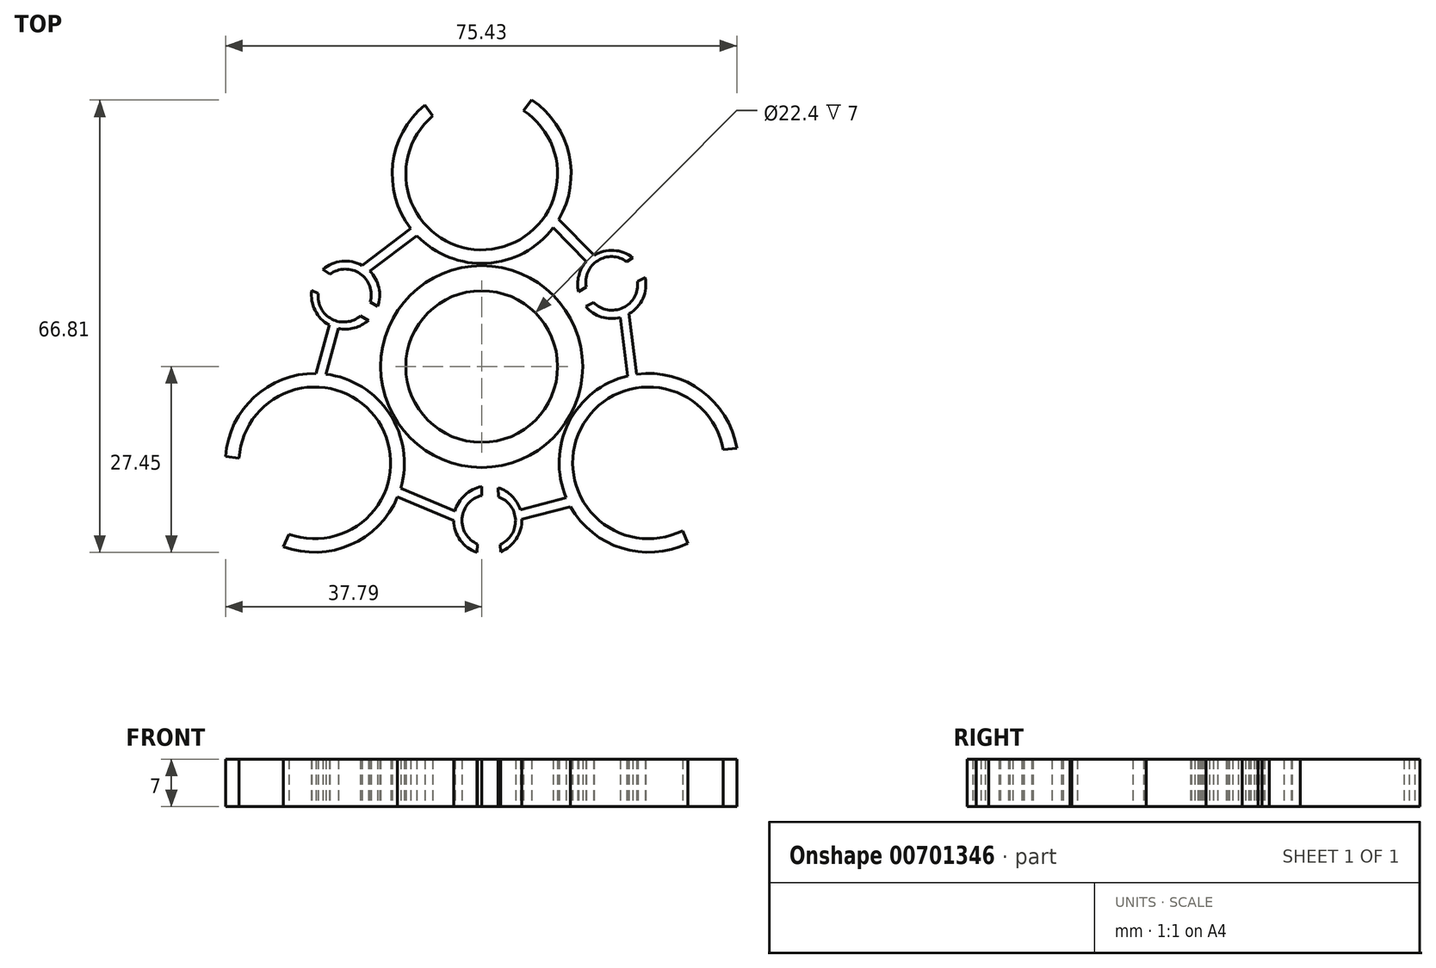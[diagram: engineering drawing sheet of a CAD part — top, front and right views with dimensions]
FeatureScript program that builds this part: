
annotation { "Feature Type Name" : "Feature", "Feature Type Description" : "" }
export const myFeature = defineFeature(function(context is Context, id is Id, definition is map)
    precondition{}
    {
        {
            var Q0;
            Q0=qCreatedBy(makeId("Top.planeOp"),FACE);
            var sketch = newSketch(context, id + "F0", { "sketchPlane" : qUnion([Q0])});
            skCircle(sketch, "E0", {"center": v(0, 0) * mm, "radius": 11.2 * mm});
            skArc(sketch, "E1", {"start": v(-7.22, 37) * mm, "mid": v(0.65, 17.25) * mm, "end": v(6.17, 37.78) * mm});
            skArc(sketch, "E2.1.0", {"start": v(-28.43, -24.75) * mm, "mid": v(-15.26, -8.06) * mm, "end": v(-35.8, -13.54) * mm});
            skArc(sketch, "E2.2.0", {"start": v(35.65, -12.25) * mm, "mid": v(14.61, -9.19) * mm, "end": v(29.63, -24.23) * mm});
            skArc(sketch, "E3", {"start": v(-8.4, 38.62) * mm, "mid": v(1.44, 15.3) * mm, "end": v(6, 40.2) * mm});
            skArc(sketch, "E4.1.0", {"start": v(-29.24, -26.58) * mm, "mid": v(-13.52, -7.08) * mm, "end": v(-37.79, -13.28) * mm});
            skArc(sketch, "E4.2.0", {"start": v(37.64, -12.04) * mm, "mid": v(12.9, -8.16) * mm, "end": v(30.4, -26.09) * mm});
            skCircle(sketch, "E5", {"center": v(0, 0) * mm, "radius": 14.9 * mm});
            skPoint(sketch, "E6", {"position": v(-6.05, 40.16) * mm});
            skPoint(sketch, "E7", {"position": v(3.9, 41.04) * mm});
            skPoint(sketch, "E8", {"position": v(3.9, 38.93) * mm});
            skPoint(sketch, "E9", {"position": v(-5.15, 38.37) * mm});
            skPoint(sketch, "E10.1.0", {"position": v(-31.76, -25.32) * mm});
            skPoint(sketch, "E10.1.1", {"position": v(-30.66, -23.65) * mm});
            skPoint(sketch, "E10.1.2", {"position": v(-35.67, -16.08) * mm});
            skPoint(sketch, "E10.1.3", {"position": v(-37.5, -17.14) * mm});
            skPoint(sketch, "E10.2.0", {"position": v(37.8, -14.84) * mm});
            skPoint(sketch, "E10.2.1", {"position": v(35.81, -14.72) * mm});
            skPoint(sketch, "E10.2.2", {"position": v(31.76, -22.85) * mm});
            skPoint(sketch, "E10.2.3", {"position": v(33.59, -23.9) * mm});
            skArc(sketch, "E11", {"start": v(-25.08, 11.26) * mm, "mid": v(-22.45, 6.1) * mm, "end": v(-16.7, 6.83) * mm});
            skArc(sketch, "E12.1.0", {"start": v(2.8, -27.35) * mm, "mid": v(5.94, -22.5) * mm, "end": v(2.44, -17.88) * mm});
            skArc(sketch, "E12.2.0", {"start": v(15.35, 8.86) * mm, "mid": v(21.39, 7.6) * mm, "end": v(24.12, 13.12) * mm});
            skLineSegment(sketch, "E13", {"start": v(-22.5, 6.14) * mm, "end": v(-24.46, -1.02) * mm});
            skLineSegment(sketch, "E14", {"start": v(-21.16, 5.64) * mm, "end": v(-23, -1.11) * mm});
            skLineSegment(sketch, "E15.1.0", {"start": v(5.7, -21.14) * mm, "end": v(12.47, -19.37) * mm});
            skLineSegment(sketch, "E15.1.1", {"start": v(5.94, -22.56) * mm, "end": v(13.1, -20.67) * mm});
            skLineSegment(sketch, "E15.2.0", {"start": v(15.46, 15.5) * mm, "end": v(10.54, 20.48) * mm});
            skLineSegment(sketch, "E15.2.1", {"start": v(16.56, 16.42) * mm, "end": v(11.35, 21.7) * mm});
            skLineSegment(sketch, "E16", {"start": v(-17.62, 14.94) * mm, "end": v(-10.45, 20.37) * mm});
            skLineSegment(sketch, "E17", {"start": v(-16.52, 14.1) * mm, "end": v(-9.56, 19.32) * mm});
            skLineSegment(sketch, "E18.1.0", {"start": v(-4.13, -22.73) * mm, "end": v(-12.42, -19.24) * mm});
            skLineSegment(sketch, "E18.1.1", {"start": v(-3.95, -21.36) * mm, "end": v(-11.96, -17.94) * mm});
            skLineSegment(sketch, "E18.2.0", {"start": v(21.75, 7.79) * mm, "end": v(22.87, -1.13) * mm});
            skLineSegment(sketch, "E18.2.1", {"start": v(20.48, 7.26) * mm, "end": v(21.51, -1.39) * mm});
            skPoint(sketch, "E19", {"position": v(-0.7, -27.45) * mm});
            skPoint(sketch, "E20", {"position": v(2.8, -27.35) * mm});
            skPoint(sketch, "E21", {"position": v(0, -17.73) * mm});
            skPoint(sketch, "E22", {"position": v(2.44, -17.88) * mm});
            skPoint(sketch, "E23.1.0", {"position": v(14.27, 11.06) * mm});
            skPoint(sketch, "E23.1.1", {"position": v(15.35, 8.86) * mm});
            skPoint(sketch, "E23.1.2", {"position": v(22.29, 16.09) * mm});
            skPoint(sketch, "E23.1.3", {"position": v(24.12, 13.12) * mm});
            skPoint(sketch, "E23.2.0", {"position": v(-16.7, 6.83) * mm});
            skPoint(sketch, "E23.2.1", {"position": v(-15.35, 8.86) * mm});
            skPoint(sketch, "E23.2.2", {"position": v(-25.08, 11.26) * mm});
            skPoint(sketch, "E23.2.3", {"position": v(-23.42, 14.33) * mm});
            skArc(sketch, "E24.trimOffspring", {"start": v(-15.35, 8.86) * mm, "mid": v(-17.27, 14.72) * mm, "end": v(-23.42, 14.33) * mm});
            skArc(sketch, "E25.trimOffspring", {"start": v(22.29, 16.09) * mm, "mid": v(16.51, 16.39) * mm, "end": v(14.27, 11.06) * mm});
            skArc(sketch, "E26.trimOffspring", {"start": v(0, -17.73) * mm, "mid": v(-4.12, -22.32) * mm, "end": v(-0.7, -27.45) * mm});
            skLineSegment(sketch, "E27", {"start": v(-23.42, 14.33) * mm, "end": v(-22.39, 13.63) * mm});
            skArc(sketch, "E28", {"start": v(-16.46, 9.53) * mm, "mid": v(-17.95, 13.72) * mm, "end": v(-22.39, 13.63) * mm});
            skLineSegment(sketch, "E29", {"start": v(-16.46, 9.53) * mm, "end": v(-15.35, 8.86) * mm});
            skLineSegment(sketch, "E30", {"start": v(-25.08, 11.26) * mm, "end": v(-24.1, 10.78) * mm});
            skArc(sketch, "E31", {"start": v(-24.1, 10.78) * mm, "mid": v(-22.12, 7.01) * mm, "end": v(-17.9, 7.49) * mm});
            skLineSegment(sketch, "E32", {"start": v(-17.9, 7.49) * mm, "end": v(-16.7, 6.83) * mm});
            skArc(sketch, "E33.1.0", {"start": v(-0.02, -19.03) * mm, "mid": v(-2.9, -22.4) * mm, "end": v(-0.6, -26.2) * mm});
            skLineSegment(sketch, "E33.1.1", {"start": v(-0.7, -27.45) * mm, "end": v(-0.6, -26.2) * mm});
            skLineSegment(sketch, "E33.1.2", {"start": v(-0.02, -19.03) * mm, "end": v(0, -17.73) * mm});
            skLineSegment(sketch, "E33.1.3", {"start": v(2.46, -19.24) * mm, "end": v(2.44, -17.88) * mm});
            skArc(sketch, "E33.1.4", {"start": v(2.72, -26.26) * mm, "mid": v(4.99, -22.66) * mm, "end": v(2.46, -19.24) * mm});
            skLineSegment(sketch, "E33.1.5", {"start": v(2.8, -27.35) * mm, "end": v(2.72, -26.26) * mm});
            skArc(sketch, "E33.2.0", {"start": v(16.49, 9.5) * mm, "mid": v(20.85, 8.69) * mm, "end": v(23, 12.57) * mm});
            skLineSegment(sketch, "E33.2.1", {"start": v(24.12, 13.12) * mm, "end": v(23, 12.57) * mm});
            skLineSegment(sketch, "E33.2.2", {"start": v(16.49, 9.5) * mm, "end": v(15.35, 8.86) * mm});
            skLineSegment(sketch, "E33.2.3", {"start": v(15.43, 11.75) * mm, "end": v(14.27, 11.06) * mm});
            skArc(sketch, "E33.2.4", {"start": v(21.39, 15.49) * mm, "mid": v(17.13, 15.65) * mm, "end": v(15.43, 11.75) * mm});
            skLineSegment(sketch, "E33.2.5", {"start": v(22.29, 16.09) * mm, "end": v(21.39, 15.49) * mm});
            skPoint(sketch, "E34", {"position": v(-8.4, 38.62) * mm});
            skPoint(sketch, "E35", {"position": v(-7.22, 37) * mm});
            skPoint(sketch, "E36", {"position": v(6, 40.2) * mm});
            skPoint(sketch, "E37", {"position": v(6.17, 37.78) * mm});
            skPoint(sketch, "E38", {"position": v(7.4, 39.36) * mm});
            skPoint(sketch, "E39.1.0", {"position": v(-29.24, -26.58) * mm});
            skPoint(sketch, "E39.1.1", {"position": v(-28.43, -24.75) * mm});
            skPoint(sketch, "E39.1.2", {"position": v(-35.8, -13.54) * mm});
            skPoint(sketch, "E39.1.3", {"position": v(-37.79, -13.28) * mm});
            skPoint(sketch, "E39.2.0", {"position": v(37.64, -12.04) * mm});
            skPoint(sketch, "E39.2.1", {"position": v(35.65, -12.25) * mm});
            skPoint(sketch, "E39.2.2", {"position": v(29.63, -24.23) * mm});
            skPoint(sketch, "E39.2.3", {"position": v(30.4, -26.09) * mm});
            skLineSegment(sketch, "E40", {"start": v(-8.4, 38.62) * mm, "end": v(-7.22, 37) * mm});
            skLineSegment(sketch, "E41", {"start": v(7.4, 39.36) * mm, "end": v(6.17, 37.78) * mm});
            skLineSegment(sketch, "E42", {"start": v(29.63, -24.23) * mm, "end": v(30.4, -26.09) * mm});
            skLineSegment(sketch, "E43", {"start": v(35.65, -12.25) * mm, "end": v(37.64, -12.04) * mm});
            skLineSegment(sketch, "E44", {"start": v(-37.79, -13.28) * mm, "end": v(-35.8, -13.54) * mm});
            skLineSegment(sketch, "E45", {"start": v(-29.24, -26.58) * mm, "end": v(-28.43, -24.75) * mm});
            skSolve(sketch);
        }
        {
            var Q0;
            Q0=makeQuery(id+"F0.imprint","IMPRINT",FACE,{"disambiguationData":[TD([[makeQuery(id+"F0.imprint","IMPRINT",EDGE,{"derivedFrom":sQuery(id+"F0.wireOp",EDGE,"E1")}),-1.0]])]});
            var Q1;
            {var subQ0=sQuery(id+"F0.wireOp",EDGE,"E16");Q1=makeQuery(id+"F0.imprint","IMPRINT",FACE,{"disambiguationData":[TD([[makeQuery(id+"F0.imprint","IMPRINT",EDGE,{"derivedFrom":subQ0}),-1.0]])]});}
            var Q2;
            {var subQ0=sQuery(id+"F0.wireOp",EDGE,"E15.2.0");Q2=makeQuery(id+"F0.imprint","IMPRINT",FACE,{"disambiguationData":[TD([[makeQuery(id+"F0.imprint","IMPRINT",EDGE,{"derivedFrom":subQ0}),-1.0]])]});}
            var Q3;
            Q3=makeQuery(id+"F0.imprint","IMPRINT",FACE,{"disambiguationData":[TD([[makeQuery(id+"F0.imprint","IMPRINT",EDGE,{"derivedFrom":sQuery(id+"F0.wireOp",EDGE,"E0")}),-1.0]])]});
            var Q4;
            {var subQ0=sQuery(id+"F0.wireOp",EDGE,"E5");var subQ1=sQuery(id+"F0.wireOp",EDGE,"E3");var subQ2=makeQuery(id+"F0.imprint","INTERSECT",VERTEX,{"disambiguationData":[OD(0.0)],"derivedFrom":[subQ1,subQ0]});Q4=makeQuery(id+"F0.imprint","IMPRINT",FACE,{"disambiguationData":[TD([[makeQuery(id+"F0.imprint","IMPRINT",EDGE,{"disambiguationData":[TD([[subQ2,-1.0]])],"derivedFrom":subQ1}),1.0]])]});}
            var Q5;
            {var subQ0=sQuery(id+"F0.wireOp",EDGE,"E5");var subQ1=sQuery(id+"F0.wireOp",EDGE,"E4.1.0");var subQ2=makeQuery(id+"F0.imprint","INTERSECT",VERTEX,{"disambiguationData":[OD(0.0)],"derivedFrom":[subQ1,subQ0]});Q5=makeQuery(id+"F0.imprint","IMPRINT",FACE,{"disambiguationData":[TD([[makeQuery(id+"F0.imprint","IMPRINT",EDGE,{"disambiguationData":[TD([[subQ2,-1.0]])],"derivedFrom":subQ1}),1.0]])]});}
            var Q6;
            {var subQ0=sQuery(id+"F0.wireOp",EDGE,"E5");var subQ1=sQuery(id+"F0.wireOp",EDGE,"E4.2.0");var subQ2=makeQuery(id+"F0.imprint","INTERSECT",VERTEX,{"disambiguationData":[OD(0.0)],"derivedFrom":[subQ1,subQ0]});Q6=makeQuery(id+"F0.imprint","IMPRINT",FACE,{"disambiguationData":[TD([[makeQuery(id+"F0.imprint","IMPRINT",EDGE,{"disambiguationData":[TD([[subQ2,-1.0]])],"derivedFrom":subQ1}),1.0]])]});}
            var Q7;
            Q7=makeQuery(id+"F0.imprint","IMPRINT",FACE,{"disambiguationData":[TD([[makeQuery(id+"F0.imprint","IMPRINT",EDGE,{"derivedFrom":sQuery(id+"F0.wireOp",EDGE,"E2.2.0")}),-1.0]])]});
            var Q8;
            {var subQ0=sQuery(id+"F0.wireOp",EDGE,"E18.2.0");Q8=makeQuery(id+"F0.imprint","IMPRINT",FACE,{"disambiguationData":[TD([[makeQuery(id+"F0.imprint","IMPRINT",EDGE,{"derivedFrom":subQ0}),-1.0]])]});}
            var Q9;
            Q9=makeQuery(id+"F0.imprint","IMPRINT",FACE,{"disambiguationData":[TD([[makeQuery(id+"F0.imprint","IMPRINT",EDGE,{"derivedFrom":sQuery(id+"F0.wireOp",EDGE,"E33.2.0")}),-1.0]])]});
            var Q10;
            {var subQ0=sQuery(id+"F0.wireOp",EDGE,"E33.2.3");Q10=makeQuery(id+"F0.imprint","IMPRINT",FACE,{"disambiguationData":[TD([[makeQuery(id+"F0.imprint","IMPRINT",EDGE,{"derivedFrom":subQ0}),-1.0]])]});}
            var Q11;
            {var subQ2=sQuery(id+"F0.wireOp",EDGE,"E27");Q11=makeQuery(id+"F0.imprint","IMPRINT",FACE,{"disambiguationData":[TD([[makeQuery(id+"F0.imprint","IMPRINT",EDGE,{"derivedFrom":subQ2}),1.0]])]});}
            var Q12;
            {var subQ0=sQuery(id+"F0.wireOp",EDGE,"E30");Q12=makeQuery(id+"F0.imprint","IMPRINT",FACE,{"disambiguationData":[TD([[makeQuery(id+"F0.imprint","IMPRINT",EDGE,{"derivedFrom":subQ0}),-1.0]])]});}
            var Q13;
            Q13=makeQuery(id+"F0.imprint","IMPRINT",FACE,{"disambiguationData":[TD([[makeQuery(id+"F0.imprint","IMPRINT",EDGE,{"derivedFrom":sQuery(id+"F0.wireOp",EDGE,"E2.1.0")}),-1.0]])]});
            var Q14;
            {var subQ0=sQuery(id+"F0.wireOp",EDGE,"E13");Q14=makeQuery(id+"F0.imprint","IMPRINT",FACE,{"disambiguationData":[TD([[makeQuery(id+"F0.imprint","IMPRINT",EDGE,{"derivedFrom":subQ0}),1.0]])]});}
            var Q15;
            {var subQ0=sQuery(id+"F0.wireOp",EDGE,"E18.1.0");Q15=makeQuery(id+"F0.imprint","IMPRINT",FACE,{"disambiguationData":[TD([[makeQuery(id+"F0.imprint","IMPRINT",EDGE,{"derivedFrom":subQ0}),-1.0]])]});}
            var Q16;
            Q16=makeQuery(id+"F0.imprint","IMPRINT",FACE,{"disambiguationData":[TD([[makeQuery(id+"F0.imprint","IMPRINT",EDGE,{"derivedFrom":sQuery(id+"F0.wireOp",EDGE,"E33.1.0")}),-1.0]])]});
            var Q17;
            {var subQ0=sQuery(id+"F0.wireOp",EDGE,"E15.1.0");Q17=makeQuery(id+"F0.imprint","IMPRINT",FACE,{"disambiguationData":[TD([[makeQuery(id+"F0.imprint","IMPRINT",EDGE,{"derivedFrom":subQ0}),-1.0]])]});}
            var Q18;
            {var subQ0=sQuery(id+"F0.wireOp",EDGE,"E33.1.3");Q18=makeQuery(id+"F0.imprint","IMPRINT",FACE,{"disambiguationData":[TD([[makeQuery(id+"F0.imprint","IMPRINT",EDGE,{"derivedFrom":subQ0}),-1.0]])]});}
            extrude(context, id + "F1", {"entities" : qUnion([Q0, Q1, Q2, Q3, Q4, Q5, Q6, Q7, Q8, Q9, Q10, Q11, Q12, Q13, Q14, Q15, Q16, Q17, Q18]), "depth" : 7 * mm, "offsetDistance" : 25 * mm});
        }
    });
